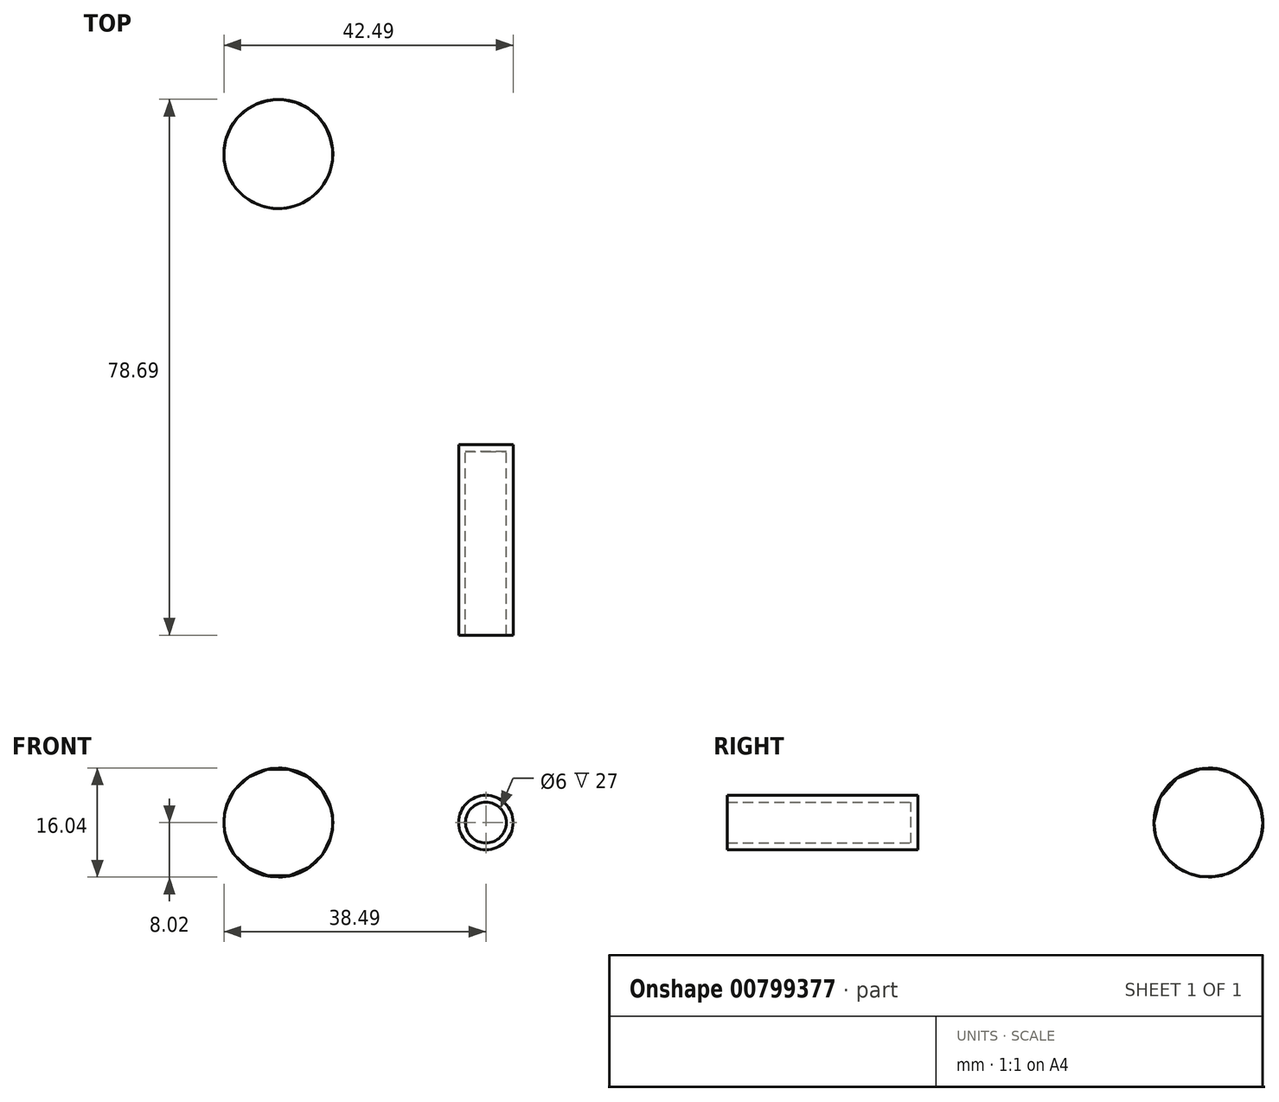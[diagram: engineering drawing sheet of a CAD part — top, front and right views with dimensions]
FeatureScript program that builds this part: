
annotation { "Feature Type Name" : "Feature", "Feature Type Description" : "" }
export const myFeature = defineFeature(function(context is Context, id is Id, definition is map)
    precondition{}
    {
        {
            var Q0;
            Q0=qCreatedBy(makeId("Front.planeOp"),FACE);
            var sketch = newSketch(context, id + "F0", { "sketchPlane" : qUnion([Q0])});
            skCircle(sketch, "E0", {"center": v(0, 0) * mm, "radius": 4 * mm});
            skSolve(sketch);
        }
        {
            var Q0;
            Q0=makeQuery(id+"F0.imprint","IMPRINT",FACE,{"disambiguationData":[TD([[makeQuery(id+"F0.imprint","IMPRINT",EDGE,{"derivedFrom":sQuery(id+"F0.wireOp",EDGE,"E0")}),1.0]])]});
            extrude(context, id + "F1", {"entities" : qUnion([Q0]), "depth" : 28 * mm, "offsetDistance" : 25 * mm});
        }
        {
            var Q0;
            Q0=makeQuery(id+"F1.opExtrude","CAP_FACE",FACE,{"disambiguationData":[OSD([sQuery(id+"F0.wireOp",EDGE,"E0")])],"isStart":false});
            shell(context, id + "F2", {"entities" : qUnion([Q0]), "thickness" : 1 * mm});
        }
        {
            var Q0;
            Q0=qCreatedBy(makeId("Top.planeOp"),FACE);
            var sketch = newSketch(context, id + "F3", { "sketchPlane" : qUnion([Q0])});
            skArc(sketch, "E1", {"start": v(-38.06, 45.26) * mm, "mid": v(-33.09, 35.08) * mm, "end": v(-22.92, 40.08) * mm});
            skLineSegment(sketch, "E2", {"start": v(-22.92, 40.08) * mm, "end": v(-38.06, 45.26) * mm});
            skSolve(sketch);
        }
        {
            var Q0;
            Q0=makeQuery(id+"F3.imprint","IMPRINT",FACE,{"disambiguationData":[TD([[makeQuery(id+"F3.imprint","IMPRINT",EDGE,{"derivedFrom":sQuery(id+"F3.wireOp",EDGE,"E1")}),1.0]])]});
            var Q1;
            Q1=sQuery(id+"F3.wireOp",EDGE,"E2");
            revolve(context, id + "F4", {"surfaceOperationType" : NewSurfaceOperationType.NEW, "entities" : qUnion([Q0]), "axis" : qUnion([Q1]), "revolveType" : RevolveType.FULL});
        }
    });
